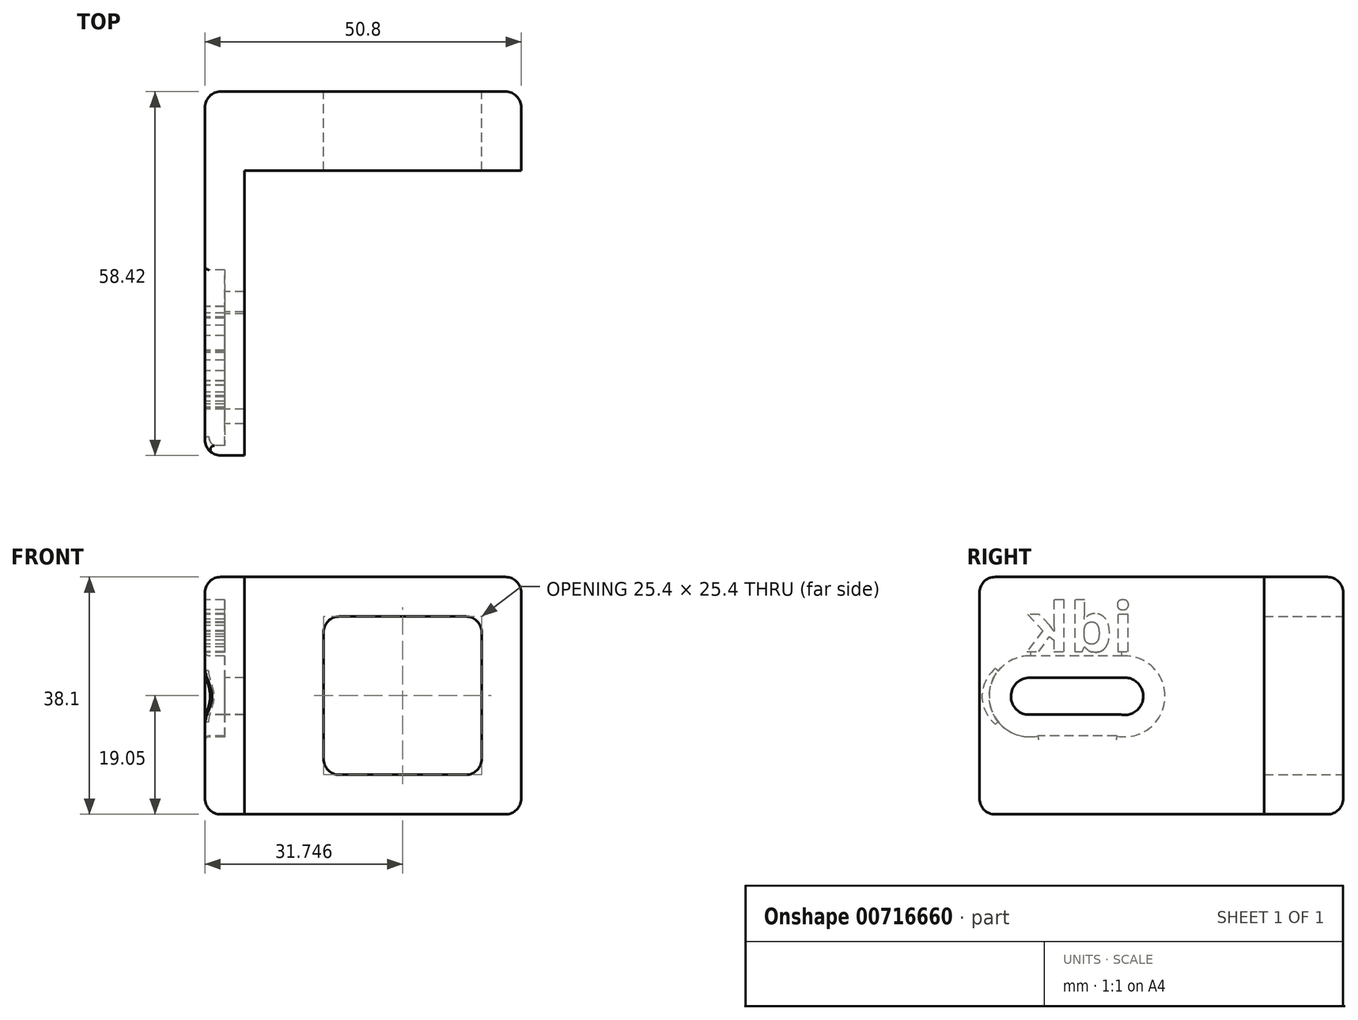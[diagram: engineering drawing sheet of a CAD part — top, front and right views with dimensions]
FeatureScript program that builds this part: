
annotation { "Feature Type Name" : "Feature", "Feature Type Description" : "" }
export const myFeature = defineFeature(function(context is Context, id is Id, definition is map)
    precondition{}
    {
        {
            var Q0;
            Q0=qCreatedBy(makeId("Front.planeOp"),FACE);
            var sketch = newSketch(context, id + "F0", { "sketchPlane" : qUnion([Q0])});
            skLineSegment(sketch, "E0.bottom", {"start": v(12.24, 12.7) * mm, "end": v(37.64, 12.7) * mm});
            skLineSegment(sketch, "E0.top", {"start": v(12.24, -12.7) * mm, "end": v(37.64, -12.7) * mm});
            skLineSegment(sketch, "E0.left", {"start": v(12.24, 12.7) * mm, "end": v(12.24, -12.7) * mm});
            skLineSegment(sketch, "E0.right", {"start": v(37.64, 12.7) * mm, "end": v(37.64, -12.7) * mm});
            skPoint(sketch, "E0.middle", {"position": v(24.94, 0) * mm});
            skLineSegment(sketch, "E1.bottom", {"start": v(5.89, 19.05) * mm, "end": v(43.99, 19.05) * mm});
            skLineSegment(sketch, "E1.top", {"start": v(5.89, -19.05) * mm, "end": v(43.99, -19.05) * mm});
            skLineSegment(sketch, "E1.left", {"start": v(5.89, 19.05) * mm, "end": v(5.89, -19.05) * mm});
            skLineSegment(sketch, "E1.right", {"start": v(43.99, 19.05) * mm, "end": v(43.99, -19.05) * mm});
            skLineSegment(sketch, "E2.bottom", {"start": v(5.89, 19.05) * mm, "end": v(-0.46, 19.05) * mm});
            skLineSegment(sketch, "E2.top", {"start": v(5.89, -19.05) * mm, "end": v(-0.46, -19.05) * mm});
            skLineSegment(sketch, "E2.right", {"start": v(-0.46, 19.05) * mm, "end": v(-0.46, -19.05) * mm});
            skLineSegment(sketch, "E3.bottom", {"start": v(-0.46, -19.05) * mm, "end": v(-6.81, -19.05) * mm});
            skLineSegment(sketch, "E3.top", {"start": v(-0.46, 19.05) * mm, "end": v(-6.81, 19.05) * mm});
            skLineSegment(sketch, "E3.left", {"start": v(-0.46, -19.05) * mm, "end": v(-0.46, 19.05) * mm});
            skLineSegment(sketch, "E3.right", {"start": v(-6.81, -19.05) * mm, "end": v(-6.81, 19.05) * mm});
            skSolve(sketch);
        }
        {
            var Q0;
            Q0=makeQuery(id+"F0.imprint","IMPRINT",FACE,{"disambiguationData":[TD([[makeQuery(id+"F0.imprint","IMPRINT",EDGE,{"derivedFrom":sQuery(id+"F0.wireOp",EDGE,"E2.bottom")}),1.0]])]});
            var Q1;
            Q1=makeQuery(id+"F0.imprint","IMPRINT",FACE,{"disambiguationData":[TD([[makeQuery(id+"F0.imprint","IMPRINT",EDGE,{"derivedFrom":sQuery(id+"F0.wireOp",EDGE,"E0.bottom")}),1.0]])]});
            extrude(context, id + "F1", {"entities" : qUnion([Q0, Q1]), "depth" : 12.7 * mm, "offsetDistance" : 25.4 * mm});
        }
        {
            var Q0;
            Q0=makeQuery(id+"F0.imprint","IMPRINT",FACE,{"disambiguationData":[TD([[makeQuery(id+"F0.imprint","IMPRINT",EDGE,{"derivedFrom":sQuery(id+"F0.wireOp",EDGE,"E3.bottom")}),-1.0]])]});
            extrude(context, id + "F2", {"entities" : qUnion([Q0]), "operationType" : NewBodyOperationType.ADD, "depth" : 58.42 * mm, "offsetDistance" : 25.4 * mm});
        }
        {
            var Q0;
            Q0=makeQuery(id+"F2.opExtrude","SWEPT_FACE",FACE,{"disambiguationData":[OSD([sQuery(id+"F0.wireOp",EDGE,"E3.right")])]});
            var sketch = newSketch(context, id + "F3", { "sketchPlane" : qUnion([Q0])});
            skCircle(sketch, "E4", {"center": v(50.34, -0.11) * mm, "radius": 3 * mm});
            skCircle(sketch, "E5", {"center": v(35.1, -0.1) * mm, "radius": 3 * mm});
            skLineSegment(sketch, "E6", {"start": v(50.97, -3.05) * mm, "end": v(35.67, -3.05) * mm});
            skLineSegment(sketch, "E7", {"start": v(50.34, 2.89) * mm, "end": v(35.36, 2.89) * mm});
            skPoint(sketch, "E8", {"position": v(58.42, 0) * mm});
            skCircle(sketch, "E9", {"center": v(35.1, -0.1) * mm, "radius": 6.5 * mm});
            skCircle(sketch, "E10", {"center": v(50.34, -0.11) * mm, "radius": 6.5 * mm});
            skLineSegment(sketch, "E11", {"start": v(34.67, 6.38) * mm, "end": v(50.55, 6.38) * mm});
            skLineSegment(sketch, "E12", {"start": v(36.37, -6.48) * mm, "end": v(49.01, -6.48) * mm});
            skText(sketch, "E13", { "text": "idk", "fontName": "OpenSans-Bold.ttf"});
            skPoint(sketch, "E14", {"position": v(53.34, -0.11) * mm});
            const initialGuessF3  = {"E13": [0.0337, 0.00707, 1, 0, 0.00789]};
            skSetInitialGuess(sketch, initialGuessF3);
            skSolve(sketch);
        }
        {
            var Q0;
            {var subQ0=sQuery(id+"F3.wireOp",EDGE,"E7");Q0=makeQuery(id+"F3.imprint","IMPRINT",FACE,{"disambiguationData":[TD([[makeQuery(id+"F3.imprint","IMPRINT",EDGE,{"derivedFrom":subQ0}),1.0]])]});}
            var Q1;
            {var subQ0=sQuery(id+"F3.wireOp",EDGE,"E5");var subQ1=makeQuery(id+"F3.imprint","INTERSECT",VERTEX,{"derivedFrom":[subQ0,sQuery(id+"F3.wireOp",EDGE,"E6")]});Q1=makeQuery(id+"F3.imprint","IMPRINT",FACE,{"disambiguationData":[TD([[makeQuery(id+"F3.imprint","IMPRINT",EDGE,{"disambiguationData":[TD([[subQ1,1.0]])],"derivedFrom":subQ0}),1.0]])]});}
            var Q2;
            {var subQ0=sQuery(id+"F3.wireOp",EDGE,"E4");var subQ1=makeQuery(id+"F3.imprint","INTERSECT",VERTEX,{"derivedFrom":[subQ0,sQuery(id+"F3.wireOp",EDGE,"E7")]});Q2=makeQuery(id+"F3.imprint","IMPRINT",FACE,{"disambiguationData":[TD([[makeQuery(id+"F3.imprint","IMPRINT",EDGE,{"disambiguationData":[TD([[subQ1,-1.0]])],"derivedFrom":subQ0}),1.0]])]});}
            var Q3;
            Q3=sQuery(id+"F3.wireOp",EDGE,"E7");
            var Q4;
            Q4=sQuery(id+"F3.wireOp",EDGE,"E5");
            var Q5;
            Q5=sQuery(id+"F3.wireOp",EDGE,"E6");
            var Q6;
            Q6=sQuery(id+"F3.wireOp",EDGE,"E4");
            extrude(context, id + "F4", {"entities" : qUnion([Q0, Q1, Q2]), "operationType" : NewBodyOperationType.REMOVE, "surfaceEntities" : qUnion([Q3, Q4, Q5, Q6]), "oppositeDirection" : true, "depth" : 6.35 * mm, "offsetDistance" : 25.4 * mm});
        }
        {
            var Q0;
            Q0=makeQuery(id+"F2.boolean.opBoolean","MERGE",EDGE,{"derivedFrom":[makeQuery(id+"F1.opExtrude","CAP_EDGE",EDGE,{"disambiguationData":[OSD([sQuery(id+"F0.wireOp",EDGE,"E1.top"),sQuery(id+"F0.wireOp",EDGE,"E2.top")])],"isStart":true}),makeQuery(id+"F2.opExtrude","CAP_EDGE",EDGE,{"disambiguationData":[OSD([sQuery(id+"F0.wireOp",EDGE,"E3.bottom")])],"isStart":true})]});
            var Q1;
            Q1=makeQuery(id+"F1.opExtrude","CAP_EDGE",EDGE,{"disambiguationData":[OSD([sQuery(id+"F0.wireOp",EDGE,"E1.right")])],"isStart":true});
            var Q2;
            Q2=makeQuery(id+"F2.boolean.opBoolean","MERGE",EDGE,{"derivedFrom":[makeQuery(id+"F1.opExtrude","CAP_EDGE",EDGE,{"disambiguationData":[OSD([sQuery(id+"F0.wireOp",EDGE,"E1.bottom"),sQuery(id+"F0.wireOp",EDGE,"E2.bottom")])],"isStart":true}),makeQuery(id+"F2.opExtrude","CAP_EDGE",EDGE,{"disambiguationData":[OSD([sQuery(id+"F0.wireOp",EDGE,"E3.top")])],"isStart":true})]});
            var Q3;
            Q3=makeQuery(id+"F2.opExtrude","SWEPT_EDGE",EDGE,{"disambiguationData":[OSD([sQuery(id+"F0.wireOp",EDGE,"E3.top"),sQuery(id+"F0.wireOp",EDGE,"E3.right")])]});
            var Q4;
            Q4=makeQuery(id+"F2.opExtrude","SWEPT_EDGE",EDGE,{"disambiguationData":[OSD([sQuery(id+"F0.wireOp",EDGE,"E3.bottom"),sQuery(id+"F0.wireOp",EDGE,"E3.right")])]});
            var Q5;
            Q5=makeQuery(id+"F2.opExtrude","CAP_EDGE",EDGE,{"disambiguationData":[OSD([sQuery(id+"F0.wireOp",EDGE,"E3.right")])],"isStart":true});
            var Q6;
            Q6=makeQuery(id+"F2.opExtrude","CAP_EDGE",EDGE,{"disambiguationData":[OSD([sQuery(id+"F0.wireOp",EDGE,"E3.right")])],"isStart":false});
            var Q7;
            Q7=makeQuery(id+"F1.opExtrude","SWEPT_EDGE",EDGE,{"disambiguationData":[OSD([sQuery(id+"F0.wireOp",EDGE,"E1.bottom"),sQuery(id+"F0.wireOp",EDGE,"E1.right")])]});
            var Q8;
            Q8=makeQuery(id+"F1.opExtrude","SWEPT_EDGE",EDGE,{"disambiguationData":[OSD([sQuery(id+"F0.wireOp",EDGE,"E1.top"),sQuery(id+"F0.wireOp",EDGE,"E1.right")])]});
            var Q9;
            Q9=makeQuery(id+"F2.opExtrude","CAP_EDGE",EDGE,{"disambiguationData":[OSD([sQuery(id+"F0.wireOp",EDGE,"E3.top")])],"isStart":false});
            var Q10;
            Q10=makeQuery(id+"F2.opExtrude","CAP_EDGE",EDGE,{"disambiguationData":[OSD([sQuery(id+"F0.wireOp",EDGE,"E3.bottom")])],"isStart":false});
            fillet(context, id + "F5", {"entities" : qUnion([Q0, Q1, Q2, Q3, Q4, Q5, Q6, Q7, Q8, Q9, Q10]), "radius" : 2.54 * mm, "tangentPropagation" : true, "allowEdgeOverflow" : false});
        }
        {
            var Q0;
            Q0=makeQuery(id+"F1.opExtrude","SWEPT_EDGE",EDGE,{"disambiguationData":[OSD([sQuery(id+"F0.wireOp",EDGE,"E0.bottom"),sQuery(id+"F0.wireOp",EDGE,"E0.left")])]});
            var Q1;
            Q1=makeQuery(id+"F1.opExtrude","SWEPT_EDGE",EDGE,{"disambiguationData":[OSD([sQuery(id+"F0.wireOp",EDGE,"E0.bottom"),sQuery(id+"F0.wireOp",EDGE,"E0.right")])]});
            var Q2;
            Q2=makeQuery(id+"F1.opExtrude","SWEPT_EDGE",EDGE,{"disambiguationData":[OSD([sQuery(id+"F0.wireOp",EDGE,"E0.top"),sQuery(id+"F0.wireOp",EDGE,"E0.right")])]});
            var Q3;
            Q3=makeQuery(id+"F1.opExtrude","SWEPT_EDGE",EDGE,{"disambiguationData":[OSD([sQuery(id+"F0.wireOp",EDGE,"E0.top"),sQuery(id+"F0.wireOp",EDGE,"E0.left")])]});
            fillet(context, id + "F6", {"entities" : qUnion([Q0, Q1, Q2, Q3]), "radius" : 2.54 * mm, "tangentPropagation" : true, "allowEdgeOverflow" : false});
        }
        {
            var Q0;
            Q0 = qSketchRegion(id + "F3", true);
            extrude(context, id + "F7", {"entities" : qUnion([Q0]), "operationType" : NewBodyOperationType.REMOVE, "oppositeDirection" : true, "depth" : 3.17 * mm, "offsetDistance" : 25.4 * mm});
        }
        {
            var Q0;
            Q0=makeQuery(id+"F7.boolean.opBoolean","COPY",EDGE,{"derivedFrom":makeQuery(id+"F7.opExtrude","CAP_EDGE",EDGE,{"disambiguationData":[OSD([sQuery(id+"F3.wireOp",EDGE,"E9")])],"isStart":true})});
            var Q1;
            Q1=makeQuery(id+"F7.boolean.opBoolean","COPY",EDGE,{"derivedFrom":makeQuery(id+"F7.opExtrude","CAP_EDGE",EDGE,{"disambiguationData":[OSD([sQuery(id+"F3.wireOp",EDGE,"E12")])],"isStart":true})});
            var Q2;
            Q2=makeQuery(id+"F7.boolean.opBoolean","COPY",EDGE,{"derivedFrom":makeQuery(id+"F7.opExtrude","CAP_EDGE",EDGE,{"disambiguationData":[OSD([sQuery(id+"F3.wireOp",EDGE,"E10")])],"isStart":true})});
            var Q3;
            Q3=makeQuery(id+"F7.boolean.opBoolean","COPY",EDGE,{"derivedFrom":makeQuery(id+"F7.opExtrude","CAP_EDGE",EDGE,{"disambiguationData":[OSD([sQuery(id+"F3.wireOp",EDGE,"E11")])],"isStart":true})});
            fillet(context, id + "F8", {"entities" : qUnion([Q0, Q1, Q2, Q3]), "radius" : 0.64 * mm, "tangentPropagation" : true, "allowEdgeOverflow" : false});
        }
    });
